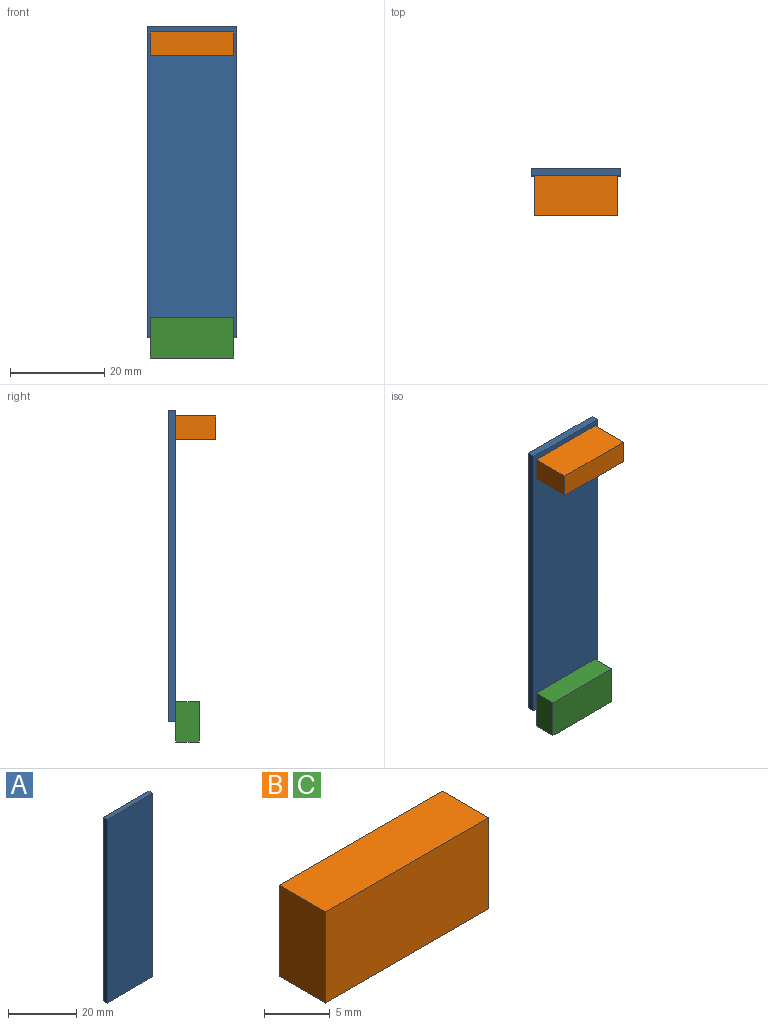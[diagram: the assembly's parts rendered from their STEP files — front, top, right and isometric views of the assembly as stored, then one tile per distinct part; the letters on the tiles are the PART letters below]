
ASSEMBLY  parts=3 mates=2
PART A: 6 faces, bbox 19.1x1.6x66 mm
  f0: plane 19.05x1.6mm, normal (0,0,-1), area 30.5mm2, adj f1,f3,f4,f5
  f1: plane 66.04x1.6mm, normal (1,0,0), area 105.7mm2, adj f0,f2,f4,f5
  f2: plane 19.05x1.6mm, normal (0,0,1), area 30.5mm2, adj f1,f3,f4,f5
  f3: plane 66.04x1.6mm, normal (-1,0,0), area 105.7mm2, adj f0,f2,f4,f5
  f4: plane 66.04x19.05mm, normal (0,-1,0), area 1258.1mm2, adj f0,f1,f2,f3
  f5: plane 66.04x19.05mm, normal (0,1,0), area 1258.1mm2, adj f0,f1,f2,f3
PART B: 6 faces, bbox 17.6x5x8.5 mm
  f0: plane 17.6x5mm, normal (0,0,1), area 88mm2, adj f1,f3,f4,f5
  f1: plane 8.5x5mm, normal (-1,0,0), area 42.5mm2, adj f0,f2,f4,f5
  f2: plane 17.6x5mm, normal (0,0,-1), area 88mm2, adj f1,f3,f4,f5
  f3: plane 8.5x5mm, normal (1,0,0), area 42.5mm2, adj f0,f2,f4,f5
  f4: plane 17.6x8.5mm, normal (0,-1,0), area 149.6mm2, adj f0,f1,f2,f3
  f5: plane 17.6x8.5mm, normal (0,1,0), area 149.6mm2, adj f0,f1,f2,f3
PART C: same geometry as B
PLACE A t=(-22.54,8.91,-4.65)mm
PLACE B rot(axis=(-1,0,0),90deg) t=(-12.84,-1.19,55.12)mm
PLACE C t=(-12.84,7.31,-8.9)mm
MATE parallel B.f0 <-> A.f4  axis (0,1,0) through (-4.04,7.31,60.12)mm
MATE parallel C.f5 <-> A.f4  axis (0,1,0) through (-4.04,7.31,-4.65)mm
